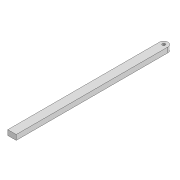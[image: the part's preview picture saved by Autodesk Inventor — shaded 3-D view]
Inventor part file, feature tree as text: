
AUTODESK INVENTOR PART (.ipt)
format: ipt  version: 2022 (Build 260153000, 153)  size: 100,864 bytes
history: native  units: mm
features: extrude x2, sketch x2
ambient origin geometry x8: Origin, YZ Plane, XZ Plane, XY Plane, X Axis, Y Axis, Z Axis, Center Point
bodies: Solid1 (feature_tree)
feature tree (4):
  extrude  "Extrusion1"  Depth=3.3mm
  extrude  "Extrusion2"  Depth=355.998mm
  sketch  "Sketch1"  dims[d0=3.3mm d1=3.3mm]
  sketch  "Sketch2"  dims[d2=10.0mm d3=355.998mm d6=6.0mm d7=0.0mm d14=3.3mm d15=57.376mm d16=10.0mm d17=0.0mm]
